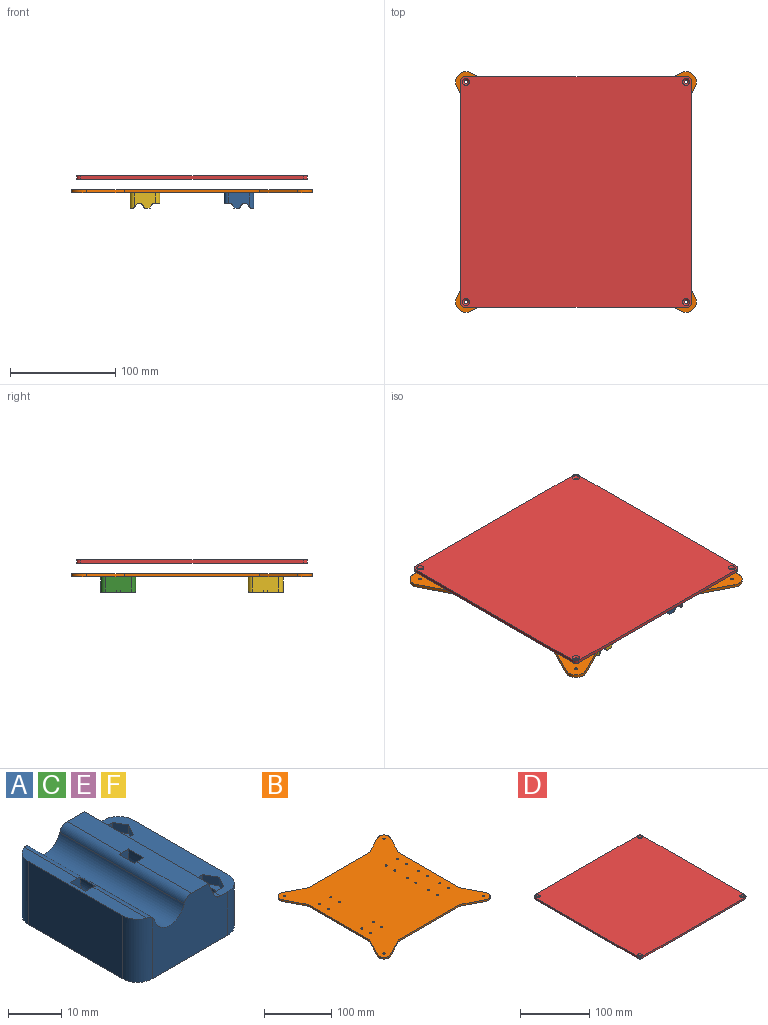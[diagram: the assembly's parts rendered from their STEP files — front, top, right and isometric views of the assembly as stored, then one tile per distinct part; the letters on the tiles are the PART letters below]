
ASSEMBLY  parts=6 mates=5
PART A: 39 faces, bbox 28x33x14.5 mm
  f0: plane 33x5.92mm, normal (0,0,1), area 151mm2, adj f3,f4,f6,f8,f9,f12,f13,f16
  f1: cylinder r=1.7mm len=8mm, axis (0,0,1), area 85.5mm2, adj f7,f21
  f2: cylinder r=1.7mm len=8mm, axis (0,0,1), area 85.5mm2, adj f7,f14
  f3: plane 25x10mm, normal (1,0,0), area 250mm2, adj f0,f7,f35,f38
  f4: plane 20x14.5mm, normal (0,1,0), area 241.3mm2, adj f0,f7,f22,f23,f25,f30,f33,f34
  f5: plane 25x14.5mm, normal (-1,0,0), area 362.5mm2, adj f7,f24,f36,f37
  f6: plane 20x14.5mm, normal (0,-1,0), area 241.3mm2, adj f0,f7,f22,f23,f25,f32,f33,f34
  f7: plane 33x28mm, normal (0,0,-1), area 892.1mm2, adj f1,f2,f3,f4,f5,f6,f35,f36
  f8: plane 2.8x2mm, normal (-0.87,-0.5,0), area 6.5mm2, adj f0,f9,f13,f14
  f9: plane 3.23x2.13mm, normal (0,-1,0), area 6.5mm2, adj f0,f8,f10,f14,f30
  f10: plane 4.36x2.8mm, normal (0.87,-0.5,0), area 9.4mm2, adj f9,f11,f14,f25,f30
  f11: plane 4.36x2.8mm, normal (0.87,0.5,0), area 9.4mm2, adj f10,f12,f14,f25,f31
  f12: plane 3.23x2.13mm, normal (0,1,0), area 6.5mm2, adj f0,f11,f13,f14,f31
  f13: plane 2.8x2mm, normal (-0.87,0.5,0), area 6.5mm2, adj f0,f8,f12,f14
  f14: plane 6.47x5.6mm, normal (0,0,1), area 18.1mm2, adj f2,f8,f9,f10,f11,f12,f13
  f15: plane 4.36x2.8mm, normal (0.87,0.5,0), area 9.4mm2, adj f16,f20,f21,f25,f32
  f16: plane 3.23x2.13mm, normal (0,1,0), area 6.5mm2, adj f0,f15,f17,f21,f32
  f17: plane 2.8x2mm, normal (-0.87,0.5,0), area 6.5mm2, adj f0,f16,f18,f21
  f18: plane 2.8x2mm, normal (-0.87,-0.5,0), area 6.5mm2, adj f0,f17,f19,f21
  f19: plane 3.23x2.13mm, normal (0,-1,0), area 6.5mm2, adj f0,f18,f20,f21,f31
  f20: plane 4.36x2.8mm, normal (0.87,-0.5,0), area 9.4mm2, adj f15,f19,f21,f25,f31
  f21: plane 6.47x5.6mm, normal (0,0,1), area 18.1mm2, adj f1,f15,f16,f17,f18,f19,f20
  f22: plane 33x4.57mm, normal (0,0,1), area 143mm2, adj f4,f6,f25,f26,f27,f29,f34
  f23: cylinder r=4mm len=33mm, axis (0,-1,0), area 348mm2, adj f4,f6,f33,f34
  f24: plane 32.56x2.69mm, normal (0,0,1), area 74.5mm2, adj f5,f26,f27,f29,f33,f36,f37
  f25: plane 33x3.27mm, normal (0.92,0,0.38), area 114.9mm2, adj f4,f6,f10,f11,f15,f20,f22,f30
  f26: cylinder r=7.73mm len=15.47mm, axis (0,1,0), area 101.2mm2, adj f22,f24,f27,f29
  f27: plane 15.47x8.24mm, normal (0,-1,0), area 53.3mm2, adj f22,f24,f26,f28,f33,f34
  f28: cylinder r=5.24mm len=10.49mm, axis (0,1,0), area 69.2mm2, adj f27,f29,f33,f34
  f29: plane 15.47x8.24mm, normal (0,1,0), area 53.3mm2, adj f22,f24,f26,f28,f33,f34
  f30: cylinder r=2mm len=3.69mm, axis (0,-1,0), area 5.8mm2, adj f0,f4,f9,f10,f25
  f31: cylinder r=2mm len=22.37mm, axis (0,-1,0), area 47mm2, adj f0,f11,f12,f19,f20,f25
  f32: cylinder r=2mm len=3.69mm, axis (0,-1,0), area 5.8mm2, adj f0,f6,f15,f16,f25
  f33: cylinder r=2mm len=33mm, axis (0,-1,0), area 84.4mm2, adj f4,f6,f23,f24,f27,f28,f29,f36
  f34: cylinder r=2mm len=33mm, axis (0,-1,0), area 84.6mm2, adj f4,f6,f22,f23,f27,f28,f29
  f35: cylinder r=4mm len=10mm, axis (0,0,-1), area 62.8mm2, adj f0,f3,f4,f7
  f36: cylinder r=4mm len=14.5mm, axis (0,0,1), area 90.9mm2, adj f4,f5,f7,f24,f33
  f37: cylinder r=4mm len=14.5mm, axis (0,0,-1), area 90.9mm2, adj f5,f6,f7,f24,f33
  f38: cylinder r=4mm len=10mm, axis (0,0,1), area 62.8mm2, adj f0,f3,f6,f7
PART B: 42 faces, bbox 228.6x228.6x3 mm
  f0: plane 228.6x228.6mm, normal (0,0,1), area 39143.5mm2, adj f2,f3,f4,f5,f6,f7,f8,f9
  f1: plane 228.6x228.6mm, normal (0,0,-1), area 39143.5mm2, adj f2,f3,f4,f5,f6,f7,f8,f9
  f2: cylinder r=1.5mm len=3mm, axis (0,0,-1), area 28.3mm2, adj f0,f1
  f3: cylinder r=1.5mm len=3mm, axis (0,0,-1), area 28.3mm2, adj f0,f1
  f4: cylinder r=1.5mm len=3mm, axis (0,0,-1), area 28.3mm2, adj f0,f1
  f5: cylinder r=1.5mm len=3mm, axis (0,0,-1), area 28.3mm2, adj f0,f1
  f6: cylinder r=1.5mm len=3mm, axis (0,0,1), area 28.3mm2, adj f0,f1
  f7: cylinder r=1.5mm len=3mm, axis (0,0,1), area 28.3mm2, adj f0,f1
  f8: cylinder r=1.5mm len=3mm, axis (0,0,1), area 28.3mm2, adj f0,f1
  f9: cylinder r=1.5mm len=3mm, axis (0,0,1), area 28.3mm2, adj f0,f1
  f10: cylinder r=1.5mm len=3mm, axis (0,0,1), area 28.3mm2, adj f0,f1
  f11: cylinder r=1.5mm len=3mm, axis (0,0,1), area 28.3mm2, adj f0,f1
  f12: cylinder r=1.5mm len=3mm, axis (0,0,1), area 28.3mm2, adj f0,f1
  f13: cylinder r=1.5mm len=3mm, axis (0,0,1), area 28.3mm2, adj f0,f1
  f14: cylinder r=1.5mm len=3mm, axis (0,0,1), area 28.3mm2, adj f0,f1
  f15: cylinder r=1.5mm len=3mm, axis (0,0,1), area 28.3mm2, adj f0,f1
  f16: cylinder r=1.5mm len=3mm, axis (0,0,1), area 28.3mm2, adj f0,f1
  f17: cylinder r=1.5mm len=3mm, axis (0,0,1), area 28.3mm2, adj f0,f1
  f18: cylinder r=1.5mm len=3mm, axis (0,0,1), area 28.3mm2, adj f0,f1
  f19: cylinder r=1.5mm len=3mm, axis (0,0,1), area 28.3mm2, adj f0,f1
  f20: cylinder r=1.5mm len=3mm, axis (0,0,1), area 28.3mm2, adj f0,f1
  f21: cylinder r=1.5mm len=3mm, axis (0,0,1), area 28.3mm2, adj f0,f1
  f22: cylinder r=1.5mm len=3mm, axis (0,0,1), area 28.3mm2, adj f0,f1
  f23: cylinder r=1.5mm len=3mm, axis (0,0,1), area 28.3mm2, adj f0,f1
  f24: cylinder r=1.5mm len=3mm, axis (0,0,1), area 28.3mm2, adj f0,f1
  f25: cylinder r=1.5mm len=3mm, axis (0,0,1), area 28.3mm2, adj f0,f1
  f26: cylinder r=9.8mm len=14.27mm, axis (0,0,1), area 74mm2, adj f0,f1,f27,f41
  f27: plane 35.61x18.22mm, normal (-0.89,-0.46,0), area 120mm2, adj f0,f1,f26,f28
  f28: plane 128.86x3mm, normal (-1,0,0), area 386.6mm2, adj f0,f1,f27,f29
  f29: plane 35.61x18.22mm, normal (-0.89,0.46,0), area 120mm2, adj f0,f1,f28,f30
  f30: cylinder r=9.8mm len=14.27mm, axis (0,0,1), area 74mm2, adj f0,f1,f29,f31
  f31: plane 35.61x18.22mm, normal (0.46,-0.89,0), area 120mm2, adj f0,f1,f30,f32
  f32: plane 128.86x3mm, normal (0,-1,0), area 386.6mm2, adj f0,f1,f31,f33
  f33: plane 35.61x18.22mm, normal (-0.46,-0.89,0), area 120mm2, adj f0,f1,f32,f34
  f34: cylinder r=9.8mm len=14.27mm, axis (0,0,1), area 74mm2, adj f0,f1,f33,f35
  f35: plane 35.61x18.22mm, normal (0.89,0.46,0), area 120mm2, adj f0,f1,f34,f36
  f36: plane 128.86x3mm, normal (1,0,0), area 386.6mm2, adj f0,f1,f35,f37
  f37: plane 35.61x18.22mm, normal (0.89,-0.46,0), area 120mm2, adj f0,f1,f36,f38
  f38: cylinder r=9.8mm len=14.27mm, axis (0,0,1), area 74mm2, adj f0,f1,f37,f39
  f39: plane 35.61x18.22mm, normal (-0.46,0.89,0), area 120mm2, adj f0,f1,f38,f40
  f40: plane 128.86x3mm, normal (0,1,0), area 386.6mm2, adj f0,f1,f39,f41
  f41: plane 35.61x18.22mm, normal (0.46,0.89,0), area 120mm2, adj f0,f1,f26,f40
PART C: same geometry as A
PART D: 18 faces, bbox 219x219x3 mm
  f0: plane 211x3mm, normal (1,0,0), area 633mm2, adj f4,f5,f14,f17
  f1: plane 211x3mm, normal (0,1,0), area 633mm2, adj f4,f5,f14,f15
  f2: plane 211x3mm, normal (-1,0,0), area 633mm2, adj f4,f5,f15,f16
  f3: plane 211x3mm, normal (0,-1,0), area 633mm2, adj f4,f5,f16,f17
  f4: plane 219x219mm, normal (0,0,-1), area 47906.6mm2, adj f0,f1,f2,f3,f6,f8,f10,f12
  f5: plane 219x219mm, normal (0,0,1), area 47805.4mm2, adj f0,f1,f2,f3,f7,f9,f11,f13
  f6: cylinder r=1.8mm len=3.6mm, axis (0,0,1), area 16.3mm2, adj f4,f7
  f7: cone r=1.8mm half-angle=45deg, axis (0,0,1), area 35.8mm2, adj f5,f6
  f8: cylinder r=1.8mm len=3.6mm, axis (0,0,1), area 16.3mm2, adj f4,f9
  f9: cone r=1.8mm half-angle=45deg, axis (0,0,1), area 35.8mm2, adj f5,f8
  f10: cylinder r=1.8mm len=3.6mm, axis (0,0,1), area 16.3mm2, adj f4,f11
  f11: cone r=1.8mm half-angle=45deg, axis (0,0,1), area 35.8mm2, adj f5,f10
  f12: cylinder r=1.8mm len=3.6mm, axis (0,0,1), area 16.3mm2, adj f4,f13
  f13: cone r=1.8mm half-angle=45deg, axis (0,0,1), area 35.8mm2, adj f5,f12
  f14: cylinder r=4mm len=4mm, axis (0,0,-1), area 18.8mm2, adj f0,f1,f4,f5
  f15: cylinder r=4mm len=4mm, axis (0,0,1), area 18.8mm2, adj f1,f2,f4,f5
  f16: cylinder r=4mm len=4mm, axis (0,0,-1), area 18.8mm2, adj f2,f3,f4,f5
  f17: cylinder r=4mm len=4mm, axis (0,0,1), area 18.8mm2, adj f0,f3,f4,f5
PART E: same geometry as A
PART F: same geometry as A
PLACE A rot(axis=(0,1,0),180deg) t=(-15.66,50.72,71.28)mm
PLACE B rot(axis=(0,0,-1),90deg) t=(-60.16,120.72,81.28)mm fixed
PLACE C rot(axis=(1,0,0),180deg) t=(-104.66,190.72,71.28)mm
PLACE D t=(-60.16,120.72,97.28)mm
PLACE E rot(axis=(0,1,0),180deg) t=(-15.66,190.72,71.28)mm
PLACE F rot(axis=(1,0,0),180deg) t=(-104.66,50.72,71.28)mm
MATE fastened A.f1 <-> B.f12  axis (0,0,1) through (-24.66,38.72,81.28)mm
MATE fastened D.f6 <-> B.f2  axis (0,0,-1) through (-164.66,225.22,94.28)mm
MATE fastened E.f1 <-> B.f16  axis (0,0,1) through (-24.66,178.72,81.28)mm
MATE fastened B.f18 <-> C.f2  axis (0,0,-1) through (-95.66,178.72,81.28)mm
MATE fastened F.f2 <-> B.f24  axis (0,0,1) through (-95.66,38.72,81.28)mm
